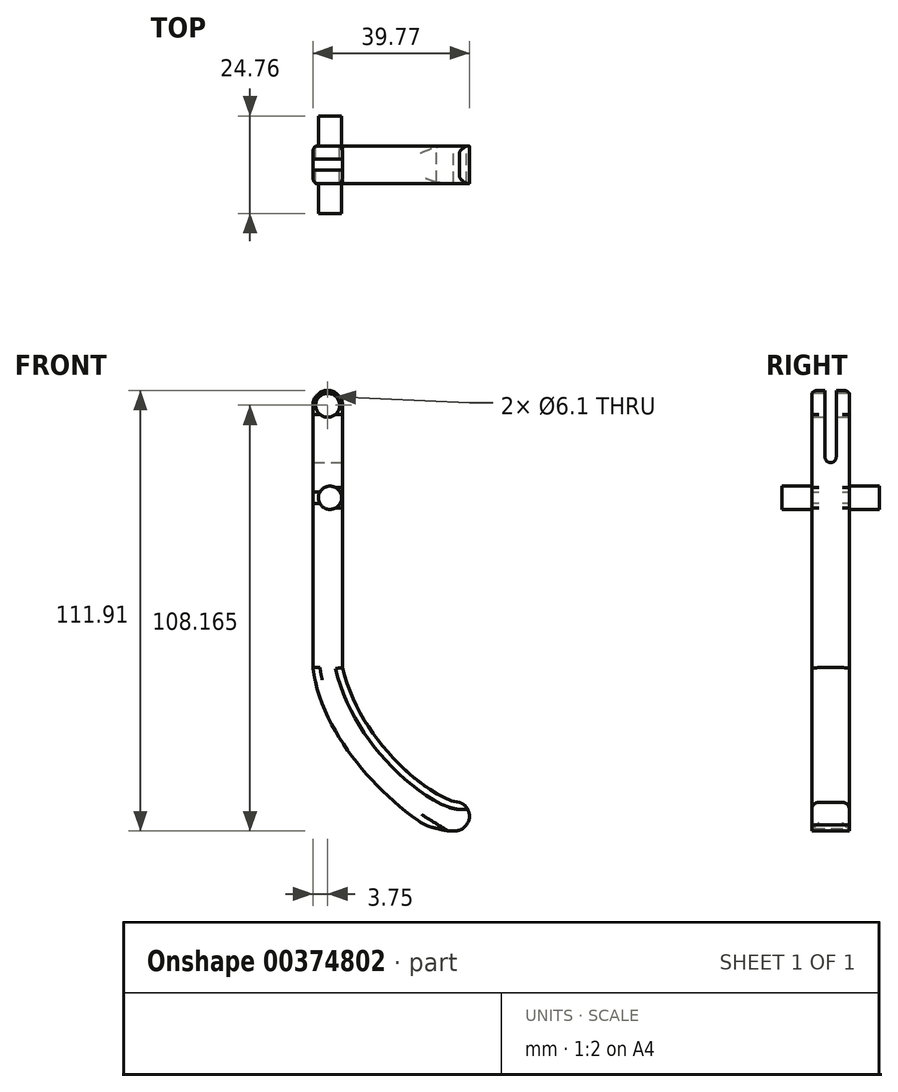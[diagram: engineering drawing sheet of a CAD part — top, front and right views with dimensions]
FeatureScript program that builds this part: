
annotation { "Feature Type Name" : "Feature", "Feature Type Description" : "" }
export const myFeature = defineFeature(function(context is Context, id is Id, definition is map)
    precondition{}
    {
        {
            var Q0;
            Q0=qCreatedBy(makeId("Front.planeOp"),FACE);
            var sketch = newSketch(context, id + "F0", { "sketchPlane" : qUnion([Q0])});
            skLineSegment(sketch, "E0", {"start": v(-1, 8.9) * mm, "end": v(-1, 0) * mm});
            skLineSegment(sketch, "E1", {"start": v(0, 8.9) * mm, "end": v(0, 0) * mm});
            skArc(sketch, "E2", {"start": v(0, 8.9) * mm, "mid": v(-0.5, 9.4) * mm, "end": v(-1, 8.9) * mm});
            skLineSegment(sketch, "E3", {"start": v(0, 8.9) * mm, "end": v(0, 8.9) * mm});
            skFitSpline(sketch, "E4", {"points": [v(0, 0) * mm, v(3.96, -4.56) * mm], "startDerivative": vector(1.96, -8.18) * mm, "endDerivative": vector(2.12, 0.03) * mm});
            skFitSpline(sketch, "E5", {"points": [v(-1, 0) * mm, v(3.62, -5.5) * mm], "startDerivative": vector(0.7, -7.6) * mm, "endDerivative": vector(1.4, -0.59) * mm});
            skArc(sketch, "E6", {"start": v(3.62, -5.5) * mm, "mid": v(3.94, -5.5) * mm, "end": v(4.2, -5.33) * mm});
            skArc(sketch, "E7", {"start": v(4.2, -5.33) * mm, "mid": v(4.28, -4.88) * mm, "end": v(3.96, -4.56) * mm});
            skCircle(sketch, "E8", {"center": v(-0.42, 5.76) * mm, "radius": 0.4 * mm});
            skCircle(sketch, "E9", {"center": v(-0.5, 8.9) * mm, "radius": 0.4 * mm});
            skFitSpline(sketch, "E10", {"points": [v(-1, 0) * mm, v(3.62, -5.5) * mm], "startDerivative": vector(9.81, -18.41) * mm, "endDerivative": vector(1.89, -0.59) * mm});
            skFitSpline(sketch, "E11", {"points": [v(-0.58, -1.33) * mm, v(2.1, -4.8) * mm], "startDerivative": vector(0.63, -2.31) * mm, "endDerivative": vector(1.82, -1.63) * mm});
            skFitSpline(sketch, "E12", {"points": [v(3.19, -5.44) * mm, v(3.75, -5.53) * mm], "startDerivative": vector(0.83, -0.3) * mm, "endDerivative": vector(0.14, 0.01) * mm});
            skFitSpline(sketch, "E13", {"points": [v(-1, 0) * mm, v(2.65, -5.24) * mm], "startDerivative": vector(1.05, -8.28) * mm, "endDerivative": vector(1.64, -1) * mm});
            skSolve(sketch);
        }
        {
            var Q0;
            Q0=makeQuery(id+"F0.imprint","IMPRINT",FACE,{"disambiguationData":[TD([[makeQuery(id+"F0.imprint","IMPRINT",EDGE,{"derivedFrom":sQuery(id+"F0.wireOp",EDGE,"E0")}),1.0]])]});
            var Q1;
            {var subQ0=sQuery(id+"F0.wireOp",EDGE,"E10");var subQ1=sQuery(id+"F0.wireOp",EDGE,"E5");var subQ2=makeQuery(id+"F0.imprint","INTERSECT",VERTEX,{"disambiguationData":[OD(0.0)],"derivedFrom":[subQ1,subQ0]});Q1=makeQuery(id+"F0.imprint","IMPRINT",FACE,{"disambiguationData":[TD([[makeQuery(id+"F0.imprint","IMPRINT",EDGE,{"disambiguationData":[TD([[subQ2,1.0]])],"derivedFrom":subQ1}),-1.0]])]});}
            var Q2;
            {var subQ0=sQuery(id+"F0.wireOp",EDGE,"E10");var subQ1=sQuery(id+"F0.wireOp",EDGE,"E5");var subQ3=makeQuery(id+"F0.imprint","INTERSECT",VERTEX,{"disambiguationData":[OD(1.0)],"derivedFrom":[subQ1,subQ0]});Q2=makeQuery(id+"F0.imprint","IMPRINT",FACE,{"disambiguationData":[TD([[makeQuery(id+"F0.imprint","IMPRINT",EDGE,{"disambiguationData":[TD([[subQ3,1.0]])],"derivedFrom":subQ1}),1.0]])]});}
            var Q3;
            {var subQ0=sQuery(id+"F0.wireOp",EDGE,"E10");var subQ1=sQuery(id+"F0.wireOp",EDGE,"E6");var subQ2=makeQuery(id+"F0.imprint","INTERSECT",VERTEX,{"derivedFrom":[subQ1,subQ0]});Q3=makeQuery(id+"F0.imprint","IMPRINT",FACE,{"disambiguationData":[TD([[makeQuery(id+"F0.imprint","IMPRINT",EDGE,{"disambiguationData":[TD([[subQ2,-1.0]])],"derivedFrom":subQ1}),-1.0]])]});}
            var Q4;
            {var subQ0=sQuery(id+"F0.wireOp",EDGE,"E10");var subQ7=sQuery(id+"F0.wireOp",EDGE,"E11");var subQ9=makeQuery(id+"F0.imprint","INTERSECT",VERTEX,{"disambiguationData":[OD(1.0)],"derivedFrom":[subQ0,subQ7]});Q4=makeQuery(id+"F0.imprint","IMPRINT",FACE,{"disambiguationData":[TD([[makeQuery(id+"F0.imprint","IMPRINT",EDGE,{"disambiguationData":[TD([[subQ9,1.0]])],"derivedFrom":subQ0}),1.0]])]});}
            var Q5;
            {var subQ3=sQuery(id+"F0.wireOp",EDGE,"E12");Q5=makeQuery(id+"F0.imprint","IMPRINT",FACE,{"disambiguationData":[TD([[makeQuery(id+"F0.imprint","IMPRINT",EDGE,{"derivedFrom":subQ3}),1.0]])]});}
            var Q6;
            {var subQ0=sQuery(id+"F0.wireOp",EDGE,"E11");Q6=makeQuery(id+"F0.imprint","IMPRINT",FACE,{"disambiguationData":[TD([[makeQuery(id+"F0.imprint","IMPRINT",EDGE,{"derivedFrom":subQ0}),-1.0]])]});}
            extrude(context, id + "F1", {"entities" : qUnion([Q0, Q1, Q2, Q3, Q4, Q5, Q6]), "endBound" : BoundingType.SYMMETRIC, "depth" : 1.27 * mm, "offsetDistance" : 25.4 * mm});
        }
        {
            var Q0;
            Q0=makeQuery(id+"F0.imprint","IMPRINT",FACE,{"disambiguationData":[TD([[makeQuery(id+"F0.imprint","IMPRINT",EDGE,{"derivedFrom":sQuery(id+"F0.wireOp",EDGE,"E8")}),1.0]])]});
            extrude(context, id + "F2", {"entities" : qUnion([Q0]), "operationType" : NewBodyOperationType.ADD, "endBound" : BoundingType.SYMMETRIC, "depth" : 3.3 * mm, "offsetDistance" : 25.4 * mm});
        }
        {
            var Q0;
            Q0=qCreatedBy(makeId("Right.planeOp"),FACE);
            cPlane(context, id + "F3", {"entities" : qUnion([Q0]), "cplaneType" : CPlaneType.OFFSET, "offset" : 25.15 * mm, "width" : 152.4 * mm, "height" : 152.4 * mm});
        }
        {
            var Q0;
            Q0=qCreatedBy(id+"F3.planeOp",FACE);
            var sketch = newSketch(context, id + "F4", { "sketchPlane" : qUnion([Q0])});
            skLineSegment(sketch, "E14", {"start": v(0.2, 9.42) * mm, "end": v(-0.2, 9.42) * mm});
            skLineSegment(sketch, "E15", {"start": v(-0.2, 9.42) * mm, "end": v(-0.2, 7.14) * mm});
            skLineSegment(sketch, "E16", {"start": v(-0.2, 7.14) * mm, "end": v(0.2, 7.14) * mm, "construction": true});
            skLineSegment(sketch, "E17", {"start": v(0.2, 7.14) * mm, "end": v(0.2, 9.42) * mm});
            skArc(sketch, "E18", {"start": v(-0.2, 7.14) * mm, "mid": v(0, 6.94) * mm, "end": v(0.2, 7.14) * mm});
            skSolve(sketch);
        }
        {
            var Q0;
            Q0=makeQuery(id+"F4.imprint","IMPRINT",FACE,{"disambiguationData":[TD([[makeQuery(id+"F4.imprint","IMPRINT",EDGE,{"derivedFrom":sQuery(id+"F4.wireOp",EDGE,"E14")}),1.0]])]});
            extrude(context, id + "F5", {"entities" : qUnion([Q0]), "operationType" : NewBodyOperationType.REMOVE, "oppositeDirection" : true, "depth" : 26.8 * mm});
        }
        {
            var Q0;
            Q0=makeQuery(id+"F1.opExtrude","SWEPT_BODY",BODY,{"disambiguationData":[OSD([sQuery(id+"F0.wireOp",EDGE,"E0"),sQuery(id+"F0.wireOp",EDGE,"E1"),sQuery(id+"F0.wireOp",EDGE,"E2"),sQuery(id+"F0.wireOp",EDGE,"E4"),sQuery(id+"F0.wireOp",EDGE,"E5"),sQuery(id+"F0.wireOp",EDGE,"E6"),sQuery(id+"F0.wireOp",EDGE,"E7"),sQuery(id+"F0.wireOp",EDGE,"E8"),sQuery(id+"F0.wireOp",EDGE,"E9")])]});
            var Q1;
            Q1=qCreatedBy(makeId("Origin.pointOp"),VERTEX);
            transform(context, id + "F6", {"entities" : qUnion([Q0]), "transformType" : TransformType.SCALE_UNIFORMLY, "scale" : 7.5, "scalePoint" : qUnion([Q1]), "makeCopy" : false});
        }
        {
            var Q0;
            Q0=makeQuery(id+"F1.opExtrude","CAP_EDGE",EDGE,{"disambiguationData":[OSD([sQuery(id+"F0.wireOp",EDGE,"E4")])],"isStart":false});
            var Q1;
            Q1=makeQuery(id+"F1.opExtrude","CAP_EDGE",EDGE,{"disambiguationData":[OSD([sQuery(id+"F0.wireOp",EDGE,"E4")])],"isStart":true});
            var Q2;
            Q2=makeQuery(id+"F1.opExtrude","CAP_EDGE",EDGE,{"disambiguationData":[OSD([sQuery(id+"F0.wireOp",EDGE,"E1")])],"isStart":false});
            var Q3;
            Q3=makeQuery(id+"F1.opExtrude","CAP_EDGE",EDGE,{"disambiguationData":[OSD([sQuery(id+"F0.wireOp",EDGE,"E1")])],"isStart":true});
            var Q4;
            Q4=makeQuery(id+"F1.opExtrude","CAP_EDGE",EDGE,{"disambiguationData":[OSD([sQuery(id+"F0.wireOp",EDGE,"E13")])],"isStart":false});
            var Q5;
            Q5=makeQuery(id+"F1.opExtrude","CAP_EDGE",EDGE,{"disambiguationData":[OSD([sQuery(id+"F0.wireOp",EDGE,"E13")])],"isStart":true});
            fillet(context, id + "F7", {"entities" : qUnion([Q0, Q1, Q2, Q3, Q4, Q5]), "radius" : 1.78 * mm, "tangentPropagation" : true, "defaultsChanged" : false, "vertexSettings" : [], "allowEdgeOverflow" : false});
        }
    });
